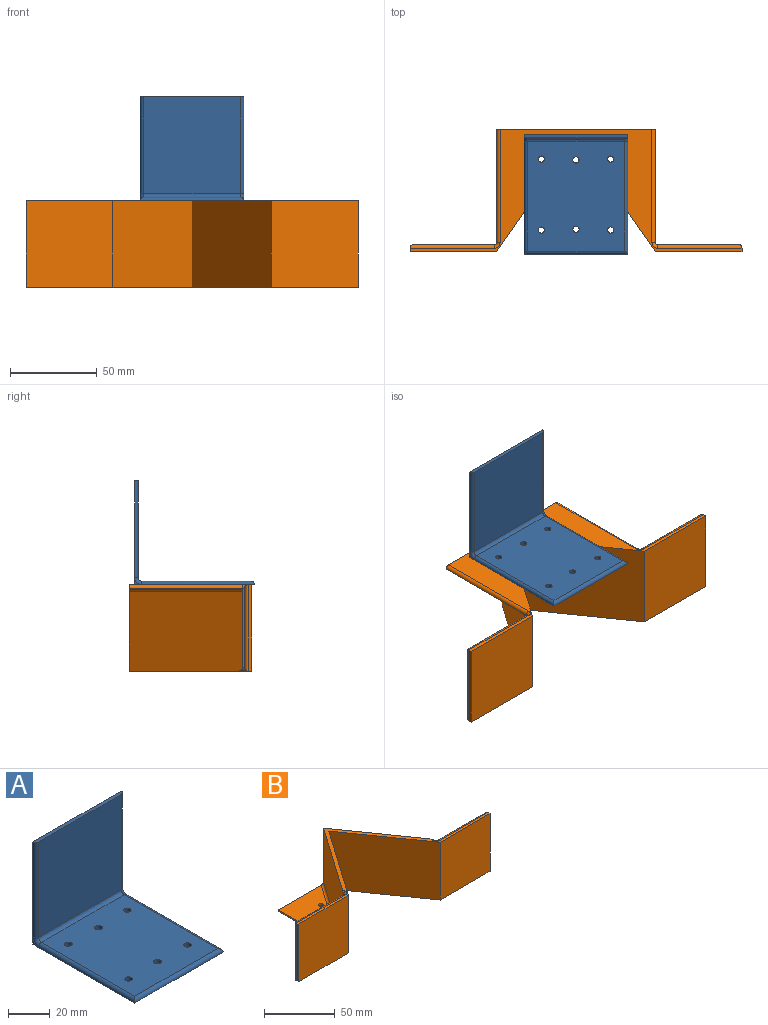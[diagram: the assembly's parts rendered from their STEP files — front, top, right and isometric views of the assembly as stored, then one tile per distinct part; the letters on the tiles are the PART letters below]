
ASSEMBLY  parts=2 mates=1
PART A: 21 faces, bbox 60x71.1x61.9 mm
  f0: plane 69.28x60mm, normal (0,0,-1), area 4095.8mm2, adj f2,f3,f4,f7,f9,f11,f15,f16
  f1: plane 63.28x56mm, normal (0,0,1), area 3482.7mm2, adj f7,f9,f11,f12,f15,f16,f17,f18
  f2: plane 4x4mm, normal (-1,0,0), area 3.4mm2, adj f0,f4,f10
  f3: plane 4x4mm, normal (1,0,0), area 3.4mm2, adj f0,f4,f13
  f4: plane 60x60mm, normal (0,1,0), area 3600mm2, adj f0,f2,f3,f5,f8,f14
  f5: plane 60x2mm, normal (0,0,1), area 118.3mm2, adj f4,f6,f8,f14
  f6: plane 56x56mm, normal (0,-1,0), area 3136mm2, adj f5,f8,f12,f14
  f7: cylinder r=2mm len=65.28mm, axis (0,-1,0), area 202.8mm2, adj f0,f1,f9,f10
  f8: cylinder r=2mm len=56mm, axis (0,0,-1), area 175.9mm2, adj f4,f5,f6,f10
  f9: cylinder r=2mm len=60mm, axis (-1,0,0), area 183.9mm2, adj f0,f1,f7,f11
  f10: torus R=4mm, axis (1,0,0), area 13.5mm2, adj f2,f7,f8,f12
  f11: cylinder r=2mm len=65.28mm, axis (0,1,0), area 202.8mm2, adj f0,f1,f9,f13
  f12: cylinder r=2mm len=56mm, axis (-1,0,0), area 175.9mm2, adj f1,f6,f10,f13
  f13: torus R=4mm, axis (1,0,0), area 13.5mm2, adj f3,f11,f12,f14
  f14: cylinder r=2mm len=56mm, axis (0,0,1), area 175.9mm2, adj f4,f5,f6,f13
  f15: cylinder r=1.8mm len=3.6mm, axis (0,0,-1), area 22.6mm2, adj f0,f1
  f16: cylinder r=1.8mm len=3.6mm, axis (0,0,-1), area 22.6mm2, adj f0,f1
  f17: cylinder r=1.8mm len=3.6mm, axis (0,0,-1), area 22.6mm2, adj f0,f1
  f18: cylinder r=1.8mm len=3.6mm, axis (0,0,-1), area 22.6mm2, adj f0,f1
  f19: cylinder r=1.8mm len=3.6mm, axis (0,0,-1), area 22.6mm2, adj f0,f1
  f20: cylinder r=1.8mm len=3.6mm, axis (0,0,-1), area 22.6mm2, adj f0,f1
PART B: 37 faces, bbox 191.8x71.7x50 mm
  f0: plane 191.77x70.53mm, normal (0,0,-1), area 3375.3mm2, adj f1,f2,f6,f7,f10,f14,f15,f17
  f1: plane 65.53x50mm, normal (0.82,-0.57,0), area 4000mm2, adj f0,f7,f8,f10
  f2: plane 91.77x50mm, normal (0,1,0), area 199.4mm2, adj f0,f3,f8,f9,f11,f16,f21,f28
  f3: plane 65.3x46mm, normal (-0.82,0.57,0), area 3665.6mm2, adj f2,f4,f8,f27,f36
  f4: plane 46x3.72mm, normal (-1,0,0), area 12.1mm2, adj f3,f20,f21,f27,f36
  f5: plane 47x46mm, normal (0,1,0), area 2162mm2, adj f20,f23,f24,f25
  f6: plane 50x2mm, normal (-1,0,0), area 100mm2, adj f0,f7,f8,f24
  f7: plane 50x50mm, normal (0,-1,0), area 2500mm2, adj f0,f1,f6,f8
  f8: plane 191.77x70.53mm, normal (0,0,1), area 665.2mm2, adj f1,f2,f3,f6,f7,f10,f11,f14
  f9: plane 61.82x43.28mm, normal (0,0,1), area 1327.6mm2, adj f2,f18,f21,f36
  f10: plane 65.53x50mm, normal (-0.82,-0.57,0), area 4000mm2, adj f0,f1,f8,f15
  f11: plane 65.3x46mm, normal (0.82,0.57,0), area 3665.6mm2, adj f2,f8,f12,f34,f35
  f12: plane 46x3.72mm, normal (1,0,0), area 12.1mm2, adj f11,f19,f28,f34,f35
  f13: plane 47x46mm, normal (0,1,0), area 2162mm2, adj f19,f30,f31,f32
  f14: plane 50x2mm, normal (1,0,0), area 100mm2, adj f0,f8,f15,f31
  f15: plane 50x50mm, normal (0,-1,0), area 2500mm2, adj f0,f8,f10,f14
  f16: plane 61.82x43.28mm, normal (0,0,1), area 1327.6mm2, adj f2,f17,f28,f35
  f17: cylinder r=1.8mm len=3.6mm, axis (0,0,-1), area 22.6mm2, adj f0,f16
  f18: cylinder r=1.8mm len=3.6mm, axis (0,0,-1), area 22.6mm2, adj f0,f9
  f19: cylinder r=1mm len=46mm, axis (0,0,-1), area 72.3mm2, adj f12,f13,f29,f33
  f20: cylinder r=1mm len=46mm, axis (0,0,-1), area 72.3mm2, adj f4,f5,f22,f26
  f21: cylinder r=2mm len=65.53mm, axis (0,-1,0), area 205.9mm2, adj f0,f2,f4,f9,f22
  f22: torus R=3mm, axis (0,0,1), area 8.5mm2, adj f0,f20,f21,f23
  f23: cylinder r=2mm len=49mm, axis (-1,0,0), area 151.7mm2, adj f0,f5,f22,f24
  f24: cylinder r=2mm len=50mm, axis (0,0,1), area 152.5mm2, adj f5,f6,f23,f25
  f25: cylinder r=2mm len=49mm, axis (1,0,0), area 151.7mm2, adj f5,f8,f24,f26
  f26: torus R=3mm, axis (0,0,1), area 8.5mm2, adj f8,f20,f25,f27
  f27: cylinder r=2mm len=3.09mm, axis (0,1,0), area 4mm2, adj f3,f4,f8,f26
  f28: cylinder r=2mm len=65.53mm, axis (0,-1,0), area 205.9mm2, adj f0,f2,f12,f16,f29
  f29: torus R=3mm, axis (0,0,1), area 8.5mm2, adj f0,f19,f28,f30
  f30: cylinder r=2mm len=49mm, axis (1,0,0), area 151.7mm2, adj f0,f13,f29,f31
  f31: cylinder r=2mm len=50mm, axis (0,0,1), area 152.5mm2, adj f13,f14,f30,f32
  f32: cylinder r=2mm len=49mm, axis (-1,0,0), area 151.7mm2, adj f8,f13,f31,f33
  f33: torus R=3mm, axis (0,0,1), area 8.5mm2, adj f8,f19,f32,f34
  f34: cylinder r=2mm len=3.09mm, axis (0,1,0), area 4mm2, adj f8,f11,f12,f33
  f35: cylinder r=2mm len=66.45mm, axis (0.57,-0.82,0), area 245.6mm2, adj f2,f11,f12,f16
  f36: cylinder r=2mm len=66.45mm, axis (-0.57,-0.82,0), area 245.6mm2, adj f2,f3,f4,f9
PLACE A t=(-30,22.57,0)mm
PLACE B rot(axis=(0,1,0),180deg) t=(0,20.57,0)mm
MATE fastened B.f18 <-> A.f19  axis (0,0,1) through (20,8.43,0)mm
